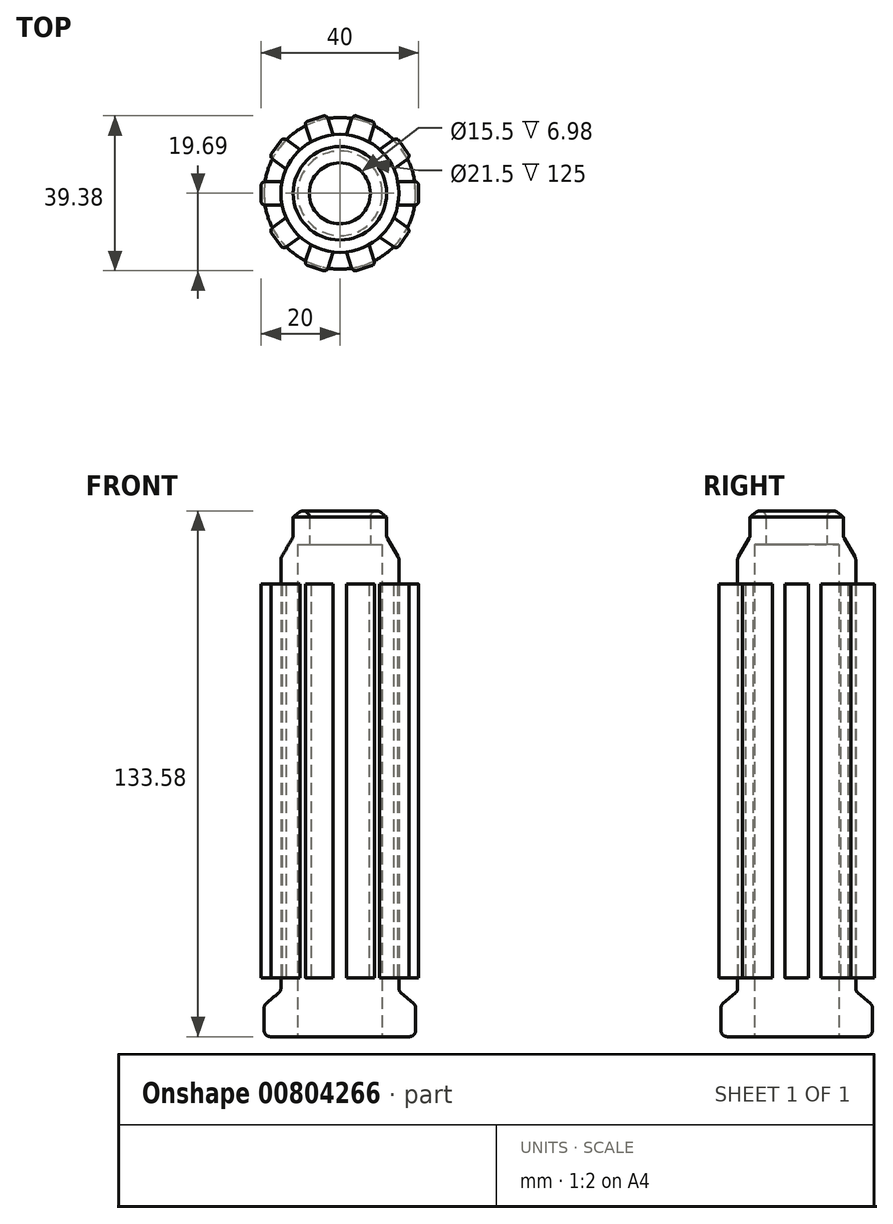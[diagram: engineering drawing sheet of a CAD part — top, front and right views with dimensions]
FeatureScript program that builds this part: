
annotation { "Feature Type Name" : "Feature", "Feature Type Description" : "" }
export const myFeature = defineFeature(function(context is Context, id is Id, definition is map)
    precondition{}
    {
        {
            var Q0;
            Q0=qCreatedBy(makeId("Front.planeOp"),FACE);
            var sketch = newSketch(context, id + "F0", { "sketchPlane" : qUnion([Q0])});
            skLineSegment(sketch, "E0", {"start": v(0, 0) * mm, "end": v(0, 40.62) * mm, "construction": true});
            skLineSegment(sketch, "E1", {"start": v(7.75, 125) * mm, "end": v(10.75, 125) * mm});
            skLineSegment(sketch, "E2", {"start": v(10.75, 125) * mm, "end": v(10.75, 0) * mm});
            skLineSegment(sketch, "E3", {"start": v(10.75, 0) * mm, "end": v(19.25, 0) * mm});
            skLineSegment(sketch, "E4", {"start": v(19.25, 0) * mm, "end": v(19.25, 8) * mm});
            skLineSegment(sketch, "E5", {"start": v(19.25, 8) * mm, "end": v(15, 11.57) * mm});
            skLineSegment(sketch, "E6", {"start": v(15, 11.57) * mm, "end": v(15, 121.57) * mm});
            skLineSegment(sketch, "E7", {"start": v(15, 121.57) * mm, "end": v(11.86, 127) * mm});
            skLineSegment(sketch, "E8", {"start": v(11.86, 127) * mm, "end": v(11.86, 132) * mm});
            skLineSegment(sketch, "E9", {"start": v(7.75, 125) * mm, "end": v(7.75, 135) * mm});
            skArc(sketch, "E10", {"start": v(11.86, 132) * mm, "mid": v(9.87, 133.59) * mm, "end": v(7.75, 135) * mm});
            skSolve(sketch);
        }
        {
            var Q0;
            Q0=makeQuery(id+"F0.imprint","IMPRINT",FACE,{"disambiguationData":[TD([[makeQuery(id+"F0.imprint","IMPRINT",EDGE,{"derivedFrom":sQuery(id+"F0.wireOp",EDGE,"E1")}),1.0]])]});
            var Q1;
            Q1=sQuery(id+"F0.wireOp",EDGE,"E0");
            revolve(context, id + "F1", {"surfaceOperationType" : NewSurfaceOperationType.NEW, "entities" : qUnion([Q0]), "axis" : qUnion([Q1]), "revolveType" : RevolveType.FULL});
        }
        {
            var Q0;
            Q0=makeQuery(id+"F1.opRevolve","SWEPT_EDGE",EDGE,{"disambiguationData":[OSD([sQuery(id+"F0.wireOp",EDGE,"E9"),sQuery(id+"F0.wireOp",EDGE,"E10")])]});
            var Q1;
            Q1=makeQuery(id+"F1.opRevolve","SWEPT_EDGE",EDGE,{"disambiguationData":[OSD([sQuery(id+"F0.wireOp",EDGE,"E7"),sQuery(id+"F0.wireOp",EDGE,"E8")])]});
            var Q2;
            Q2=makeQuery(id+"F1.opRevolve","SWEPT_EDGE",EDGE,{"disambiguationData":[OSD([sQuery(id+"F0.wireOp",EDGE,"E6"),sQuery(id+"F0.wireOp",EDGE,"E7")])]});
            var Q3;
            Q3=makeQuery(id+"F1.opRevolve","SWEPT_EDGE",EDGE,{"disambiguationData":[OSD([sQuery(id+"F0.wireOp",EDGE,"E5"),sQuery(id+"F0.wireOp",EDGE,"E6")])]});
            var Q4;
            Q4=makeQuery(id+"F1.opRevolve","SWEPT_EDGE",EDGE,{"disambiguationData":[OSD([sQuery(id+"F0.wireOp",EDGE,"E4"),sQuery(id+"F0.wireOp",EDGE,"E5")])]});
            var Q5;
            Q5=makeQuery(id+"F1.opRevolve","SWEPT_EDGE",EDGE,{"disambiguationData":[OSD([sQuery(id+"F0.wireOp",EDGE,"E3"),sQuery(id+"F0.wireOp",EDGE,"E4")])]});
            fillet(context, id + "F2", {"entities" : qUnion([Q0, Q1, Q2, Q3, Q4, Q5]), "radius" : 1.6 * mm, "tangentPropagation" : true, "allowEdgeOverflow" : false});
        }
        {
            var Q0;
            Q0=qCreatedBy(makeId("Right.planeOp"),FACE);
            cPlane(context, id + "F3", {"entities" : qUnion([Q0]), "cplaneType" : CPlaneType.OFFSET, "offset" : 20 * mm, "width" : 150 * mm, "height" : 150 * mm});
        }
        {
            var Q0;
            Q0=qCreatedBy(id+"F3.planeOp",FACE);
            var sketch = newSketch(context, id + "F4", { "sketchPlane" : qUnion([Q0])});
            skLineSegment(sketch, "E11.bottom", {"start": v(-3, 115) * mm, "end": v(3, 115) * mm});
            skLineSegment(sketch, "E11.top", {"start": v(-3, 15) * mm, "end": v(3, 15) * mm});
            skLineSegment(sketch, "E11.left", {"start": v(-3, 115) * mm, "end": v(-3, 15) * mm});
            skLineSegment(sketch, "E11.right", {"start": v(3, 115) * mm, "end": v(3, 15) * mm});
            skSolve(sketch);
        }
        {
            var Q0;
            Q0=makeQuery(id+"F4.imprint","IMPRINT",FACE,{"disambiguationData":[TD([[makeQuery(id+"F4.imprint","IMPRINT",EDGE,{"derivedFrom":sQuery(id+"F4.wireOp",EDGE,"E11.bottom")}),-1.0]])]});
            var Q1;
            Q1=makeQuery(id+"F1.opRevolve","SWEPT_FACE",FACE,{"disambiguationData":[OSD([sQuery(id+"F0.wireOp",EDGE,"E6")])]});
            extrude(context, id + "F5", {"entities" : qUnion([Q0]), "endBound" : BoundingType.UP_TO_SURFACE, "oppositeDirection" : true, "depth" : 25 * mm, "endBoundEntityFace" : qUnion([Q1]), "offsetDistance" : 25 * mm});
        }
        {
            var Q0;
            Q0=makeQuery(id+"F5.opExtrude","CAP_EDGE",EDGE,{"disambiguationData":[OSD([sQuery(id+"F4.wireOp",EDGE,"E11.left")])],"isStart":true});
            var Q1;
            Q1=makeQuery(id+"F5.opExtrude","CAP_EDGE",EDGE,{"disambiguationData":[OSD([sQuery(id+"F4.wireOp",EDGE,"E11.right")])],"isStart":true});
            fillet(context, id + "F6", {"entities" : qUnion([Q0, Q1]), "radius" : 1 * mm, "tangentPropagation" : true, "allowEdgeOverflow" : false});
        }
        {
            var Q0;
            Q0=makeQuery(id+"F5.opExtrude","SWEPT_BODY",BODY,{"disambiguationData":[OSD([sQuery(id+"F4.wireOp",EDGE,"E11.bottom"),sQuery(id+"F4.wireOp",EDGE,"E11.top"),sQuery(id+"F4.wireOp",EDGE,"E11.left"),sQuery(id+"F4.wireOp",EDGE,"E11.right")])]});
            var Q1;
            Q1=sQuery(id+"F0.wireOp",EDGE,"E0");
            circularPattern(context, id + "F7", {"entities" : qUnion([Q0]), "axis" : qUnion([Q1]), "angle" : 360 * degree, "instanceCount" : 10, "equalSpace" : true});
        }
    });
